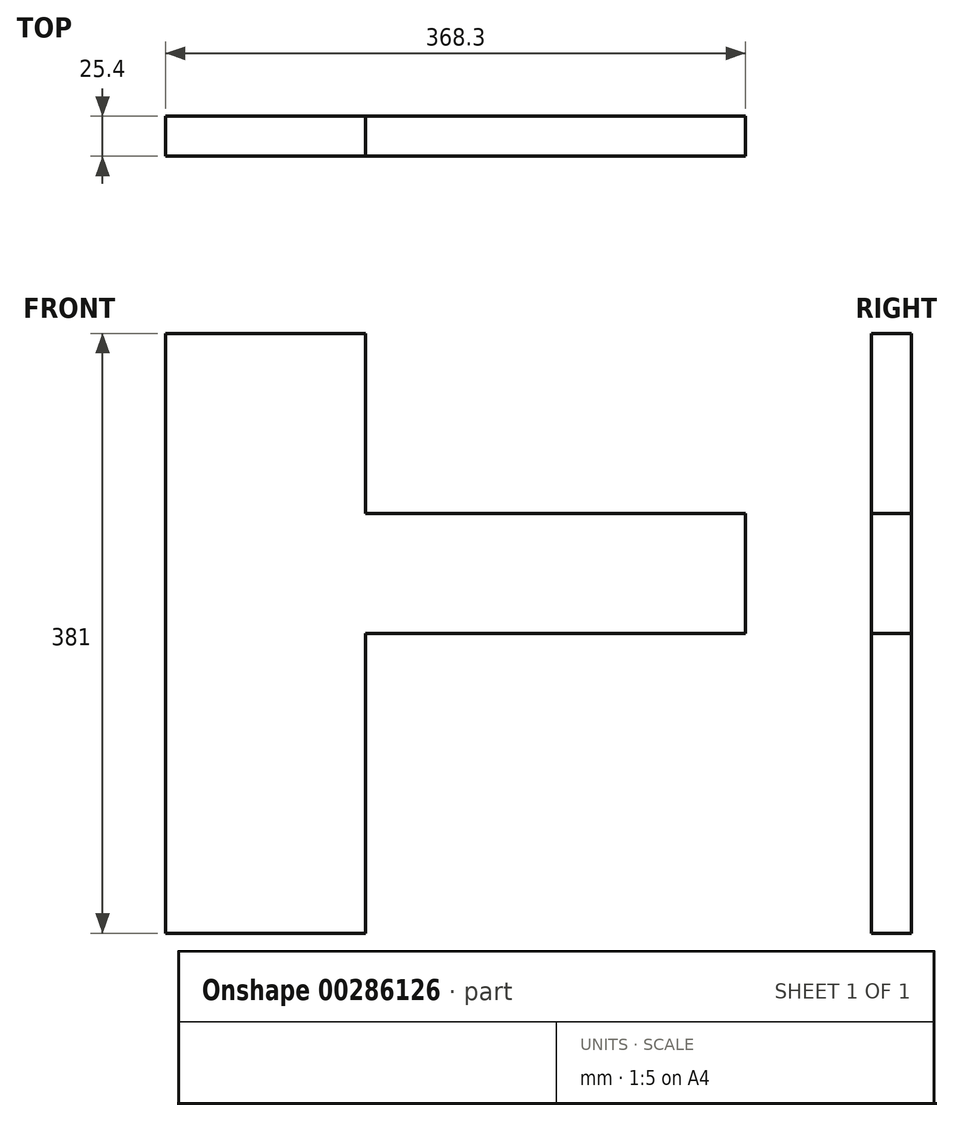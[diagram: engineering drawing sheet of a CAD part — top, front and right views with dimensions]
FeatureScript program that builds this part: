
annotation { "Feature Type Name" : "Feature", "Feature Type Description" : "" }
export const myFeature = defineFeature(function(context is Context, id is Id, definition is map)
    precondition{}
    {
        {
            var Q0;
            Q0=qCreatedBy(makeId("Front.planeOp"),FACE);
            var sketch = newSketch(context, id + "F0", { "sketchPlane" : qUnion([Q0])});
            skLineSegment(sketch, "E0", {"start": v(0, 0) * mm, "end": v(304.8, 0) * mm});
            skLineSegment(sketch, "E1", {"start": v(304.8, 0) * mm, "end": v(304.8, 76.2) * mm});
            skLineSegment(sketch, "E2", {"start": v(304.8, 76.2) * mm, "end": v(0, 76.2) * mm});
            skLineSegment(sketch, "E3", {"start": v(0, 76.2) * mm, "end": v(0, 0) * mm});
            skLineSegment(sketch, "E4.bottom", {"start": v(-63.5, -190.5) * mm, "end": v(63.5, -190.5) * mm});
            skLineSegment(sketch, "E4.top", {"start": v(-63.5, 190.5) * mm, "end": v(63.5, 190.5) * mm});
            skLineSegment(sketch, "E4.left", {"start": v(-63.5, -190.5) * mm, "end": v(-63.5, 190.5) * mm});
            skLineSegment(sketch, "E4.right", {"start": v(63.5, -190.5) * mm, "end": v(63.5, 190.5) * mm});
            skPoint(sketch, "E4.middle", {"position": v(0, 0) * mm});
            skSolve(sketch);
        }
        {
            var Q0;
            Q0 = qSketchRegion(id + "F0", true);
            extrude(context, id + "F1", {"entities" : qUnion([Q0]), "depth" : 25.4 * mm});
        }
    });
